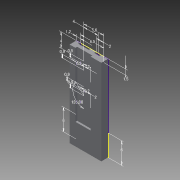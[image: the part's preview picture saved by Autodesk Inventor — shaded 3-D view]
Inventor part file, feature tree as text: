
AUTODESK INVENTOR PART (.ipt)
format: ipt  version: 2013 (Build 170138000, 138)  size: 125,440 bytes
history: native  units: mm
features: sketch x4, extrude x3, other x1
ambient origin geometry x8: Origin, YZ Plane, XZ Plane, XY Plane, X Axis, Y Axis, Z Axis, Center Point
feature tree (8):
  other  "ソリッド1"
  extrude  "押し出し1"  Depth=8.9mm
  sketch  "スケッチ2"
  sketch  "スケッチ3"
  extrude  "押し出し3"  Depth=24.0mm
  extrude  "押し出し4"  Depth=4.45mm
  sketch  "スケッチ1"
  sketch  "スケッチ4"
